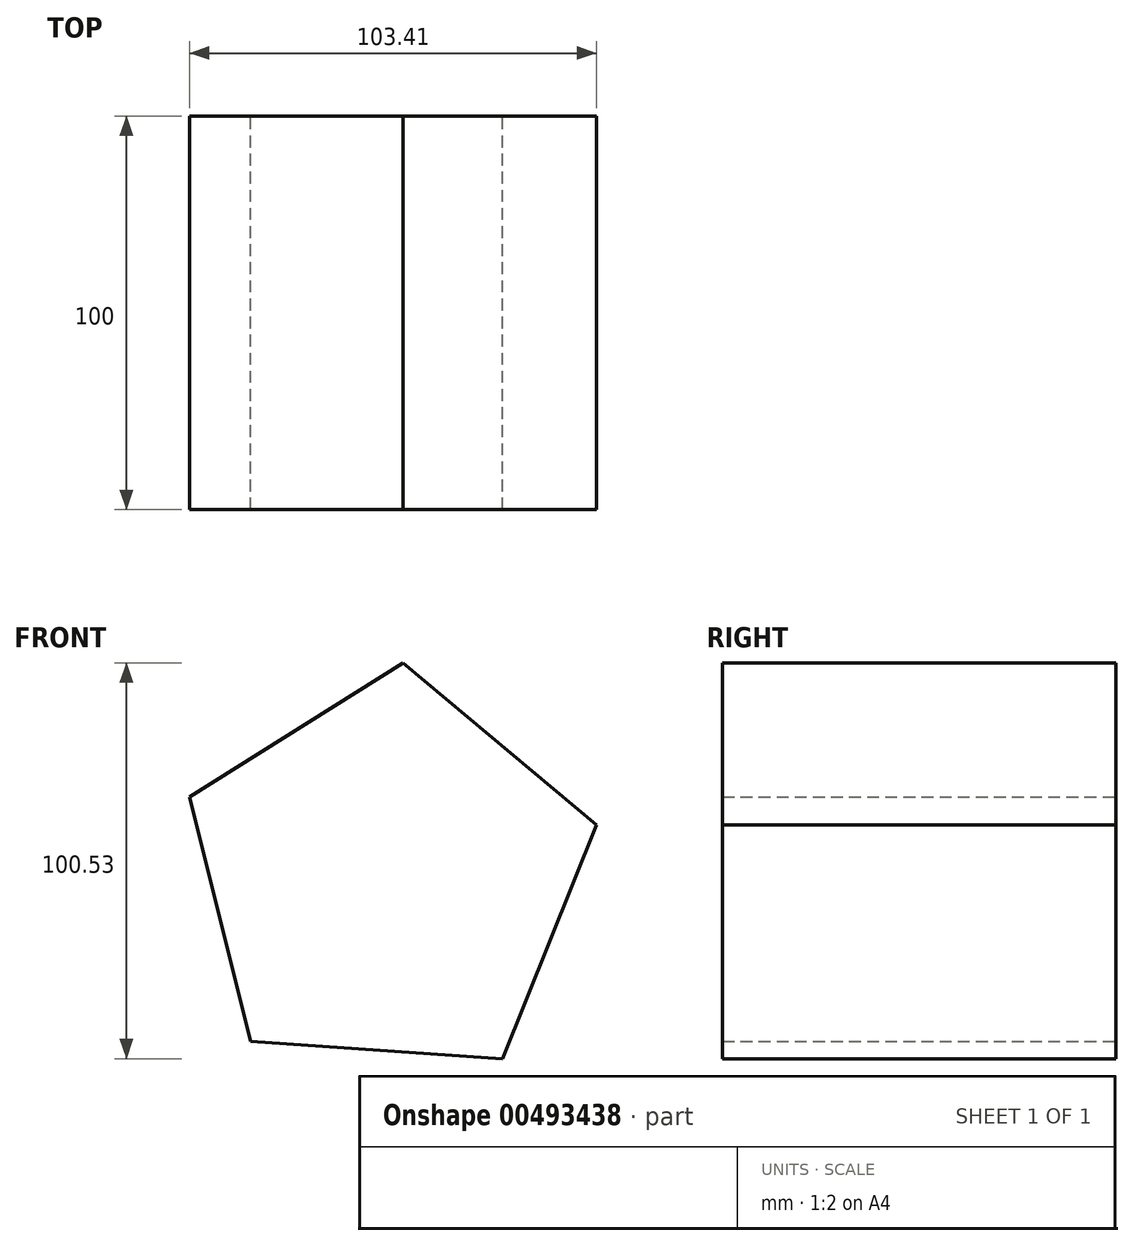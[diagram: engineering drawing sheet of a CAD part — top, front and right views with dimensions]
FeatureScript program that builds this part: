
annotation { "Feature Type Name" : "Feature", "Feature Type Description" : "" }
export const myFeature = defineFeature(function(context is Context, id is Id, definition is map)
    precondition{}
    {
        {
            var Q0;
            Q0=qCreatedBy(makeId("Front.planeOp"),FACE);
            var sketch = newSketch(context, id + "F0", { "sketchPlane" : qUnion([Q0])});
            skCircle(sketch, "E0.cCircle", {"center": v(0, 0) * mm, "radius": 54.5 * mm, "construction": true});
            skLineSegment(sketch, "E0.0", {"start": v(3.73, 54.36) * mm, "end": v(52.86, 13.25) * mm});
            skLineSegment(sketch, "E0.1", {"start": v(52.86, 13.25) * mm, "end": v(28.94, -46.17) * mm});
            skLineSegment(sketch, "E0.2", {"start": v(28.94, -46.17) * mm, "end": v(-34.97, -41.79) * mm});
            skLineSegment(sketch, "E0.3", {"start": v(-34.97, -41.79) * mm, "end": v(-50.55, 20.35) * mm});
            skLineSegment(sketch, "E0.4", {"start": v(-50.55, 20.35) * mm, "end": v(3.73, 54.36) * mm});
            skSolve(sketch);
        }
        {
            var Q0;
            Q0=makeQuery(id+"F0.imprint","IMPRINT",FACE,{"disambiguationData":[TD([[makeQuery(id+"F0.imprint","IMPRINT",EDGE,{"derivedFrom":sQuery(id+"F0.wireOp",EDGE,"E0.0")}),-1.0]])]});
            extrude(context, id + "F1", {"entities" : qUnion([Q0]), "depth" : 100 * mm});
        }
    });
